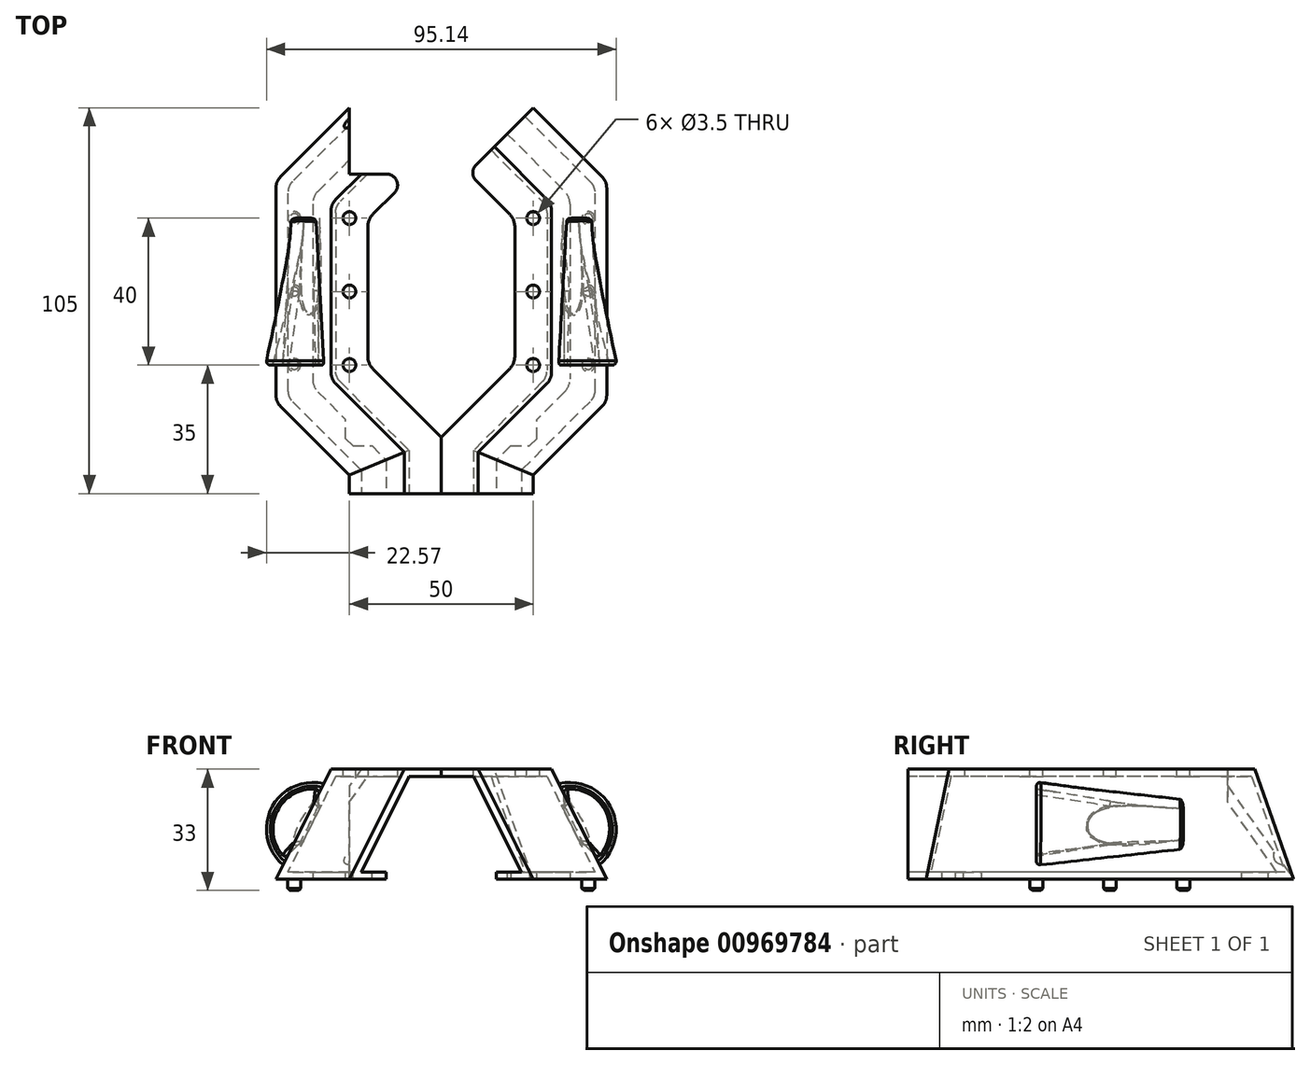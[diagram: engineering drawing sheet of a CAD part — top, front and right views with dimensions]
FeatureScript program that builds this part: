
annotation { "Feature Type Name" : "Feature", "Feature Type Description" : "" }
export const myFeature = defineFeature(function(context is Context, id is Id, definition is map)
    precondition{}
    {
        {
            var Q0;
            Q0=qCreatedBy(makeId("Front.planeOp"),FACE);
            cPlane(context, id + "F0", {"entities" : qUnion([Q0]), "cplaneType" : CPlaneType.OFFSET, "offset" : 20 * mm, "width" : 150 * mm, "height" : 150 * mm});
        }
        {
            var Q0;
            Q0=qCreatedBy(makeId("Front.planeOp"),FACE);
            cPlane(context, id + "F1", {"entities" : qUnion([Q0]), "cplaneType" : CPlaneType.OFFSET, "offset" : 20 * mm, "oppositeDirection" : true, "width" : 150 * mm, "height" : 150 * mm});
        }
        {
            var Q0;
            Q0=qCreatedBy(makeId("Top.planeOp"),FACE);
            var sketch = newSketch(context, id + "F2", { "sketchPlane" : qUnion([Q0])});
            skLineSegment(sketch, "E0.left", {"start": v(-20, 30) * mm, "end": v(-20, -30) * mm});
            skLineSegment(sketch, "E1", {"start": v(-20, 30) * mm, "end": v(0, 50) * mm});
            skLineSegment(sketch, "E2", {"start": v(-20, -30) * mm, "end": v(0, -50) * mm});
            skLineSegment(sketch, "E3", {"start": v(0, -50) * mm, "end": v(0, -55) * mm});
            skSolve(sketch);
        }
        {
            var Q0;
            Q0=qCreatedBy(makeId("Front.planeOp"),FACE);
            var sketch = newSketch(context, id + "F3", { "sketchPlane" : qUnion([Q0])});
            skLineSegment(sketch, "E4", {"start": v(-20, 0) * mm, "end": v(-5, 30) * mm});
            skLineSegment(sketch, "E5", {"start": v(-5, 30) * mm, "end": v(5, 30) * mm});
            skLineSegment(sketch, "E6", {"start": v(5, 30) * mm, "end": v(5, 28) * mm});
            skLineSegment(sketch, "E7", {"start": v(5, 28) * mm, "end": v(-3.76, 28) * mm});
            skLineSegment(sketch, "E8", {"start": v(-3.76, 28) * mm, "end": v(-16.76, 2) * mm});
            skLineSegment(sketch, "E9", {"start": v(-16.76, 2) * mm, "end": v(-10, 2) * mm});
            skLineSegment(sketch, "E10", {"start": v(-10, 2) * mm, "end": v(-10, 0) * mm});
            skLineSegment(sketch, "E11", {"start": v(-20, 0) * mm, "end": v(-10, 0) * mm});
            skSolve(sketch);
        }
        {
            var Q0;
            Q0=makeQuery(id+"F3.imprint","IMPRINT",FACE,{"disambiguationData":[TD([[makeQuery(id+"F3.imprint","IMPRINT",EDGE,{"derivedFrom":sQuery(id+"F3.wireOp",EDGE,"E4")}),-1.0]])]});
            var Q1;
            Q1=sQuery(id+"F2.wireOp",EDGE,"E0.left");
            var Q2;
            Q2=sQuery(id+"F2.wireOp",EDGE,"E1");
            var Q3;
            Q3=sQuery(id+"F2.wireOp",EDGE,"E2");
            var Q4;
            Q4=sQuery(id+"F2.wireOp",EDGE,"limmlRFK-TrjI-oLqm-ALK9-w7ykXCjVsBlW");
            var Q5;
            Q5=sQuery(id+"F2.wireOp",EDGE,"E3");
            sweep(context, id + "F4", {"profiles" : qUnion([Q0]), "path" : qUnion([Q1, Q2, Q3, Q4, Q5])});
        }
        {
            var Q0;
            Q0=qCreatedBy(id+"F0.planeOp",FACE);
            var sketch = newSketch(context, id + "F5", { "sketchPlane" : qUnion([Q0])});
            skArc(sketch, "E12", {"start": v(-6.9, 26.18) * mm, "mid": v(-21.44, 19.47) * mm, "end": v(-18.1, 3.82) * mm});
            skLineSegment(sketch, "E13", {"start": v(-6.9, 26.18) * mm, "end": v(-5, 30) * mm, "construction": true});
            skLineSegment(sketch, "E14", {"start": v(-18.1, 3.82) * mm, "end": v(-20, 0) * mm, "construction": true});
            skLineSegment(sketch, "E15", {"start": v(-6.9, 26.18) * mm, "end": v(-18.1, 3.82) * mm});
            skSolve(sketch);
        }
        {
            var Q0;
            Q0=qCreatedBy(id+"F1.planeOp",FACE);
            var sketch = newSketch(context, id + "F6", { "sketchPlane" : qUnion([Q0])});
            skArc(sketch, "E16", {"start": v(-9.15, 21.7) * mm, "mid": v(-13.4, 15.45) * mm, "end": v(-15.85, 8.3) * mm});
            skLineSegment(sketch, "E17", {"start": v(-9.15, 21.7) * mm, "end": v(-5, 30) * mm, "construction": true});
            skLineSegment(sketch, "E18", {"start": v(-15.85, 8.3) * mm, "end": v(-20, 0) * mm, "construction": true});
            skLineSegment(sketch, "E19", {"start": v(-9.15, 21.7) * mm, "end": v(-15.85, 8.3) * mm});
            skSolve(sketch);
        }
        {
            var Q0;
            Q0=makeQuery(id+"F5.imprint","IMPRINT",FACE,{"disambiguationData":[TD([[makeQuery(id+"F5.imprint","IMPRINT",EDGE,{"derivedFrom":sQuery(id+"F5.wireOp",EDGE,"E12")}),1.0]])]});
            var Q1;
            Q1=makeQuery(id+"F6.imprint","IMPRINT",FACE,{"disambiguationData":[TD([[makeQuery(id+"F6.imprint","IMPRINT",EDGE,{"derivedFrom":sQuery(id+"F6.wireOp",EDGE,"E16")}),1.0]])]});
            loft(context, id + "F7", {"operationType" : NewBodyOperationType.ADD, "sheetProfilesArray" : [{ "sheetProfileEntities" : qUnion([Q0]) }, { "sheetProfileEntities" : qUnion([Q1]) }]});
        }
        {
            var Q0;
            Q0=makeQuery(id+"F7.opLoft","CAP_FACE",FACE,{"disambiguationData":[OSD([makeQuery(id+"F5.imprint","IMPRINT",FACE,{"disambiguationData":[TD([[makeQuery(id+"F5.imprint","IMPRINT",EDGE,{"derivedFrom":sQuery(id+"F5.wireOp",EDGE,"E12")}),1.0]])]})])],"isStart":true});
            var sketch = newSketch(context, id + "F8", { "sketchPlane" : qUnion([Q0])});
            skArc(sketch, "E20", {"start": v(-7.8, 24.4) * mm, "mid": v(-19.66, 18.58) * mm, "end": v(-17.2, 5.6) * mm});
            skLineSegment(sketch, "E21", {"start": v(-17.2, 5.6) * mm, "end": v(-18.1, 3.82) * mm, "construction": true});
            skLineSegment(sketch, "E22", {"start": v(-7.8, 24.4) * mm, "end": v(-6.9, 26.18) * mm, "construction": true});
            skSolve(sketch);
        }
        {
            var Q0;
            Q0=qCreatedBy(id+"F1.planeOp",FACE);
            var sketch = newSketch(context, id + "F9", { "sketchPlane" : qUnion([Q0])});
            skArc(sketch, "E23", {"start": v(-12.05, 11.42) * mm, "mid": v(-8.48, 14.1) * mm, "end": v(-8.48, 18.58) * mm});
            skLineSegment(sketch, "E24", {"start": v(-12.05, 11.42) * mm, "end": v(-12.05, 8.3) * mm, "construction": true});
            skLineSegment(sketch, "E25", {"start": v(-8.48, 18.58) * mm, "end": v(-8.48, 21.7) * mm, "construction": true});
            skLineSegment(sketch, "E26", {"start": v(-12.05, 11.42) * mm, "end": v(-8.48, 18.58) * mm});
            skSolve(sketch);
        }
        {
            var Q1;
            {var subQ0=sQuery(id+"F8.wireOp",EDGE,"E20");Q1=makeQuery(id+"F8.imprint","IMPRINT",FACE,{"disambiguationData":[TD([[makeQuery(id+"F8.imprint","IMPRINT",EDGE,{"derivedFrom":subQ0}),1.0]])]});}
            var Q2;
            Q2=makeQuery(id+"F9.imprint","IMPRINT",FACE,{"disambiguationData":[TD([[makeQuery(id+"F9.imprint","IMPRINT",EDGE,{"derivedFrom":sQuery(id+"F9.wireOp",EDGE,"E23")}),1.0]])]});
            loft(context, id + "F10", {"operationType" : NewBodyOperationType.REMOVE, "sheetProfilesArray" : [{ "sheetProfileEntities" : qUnion([Q1]) }, { "sheetProfileEntities" : qUnion([Q2]) }]});
        }
        {
            var Q0;
            {var subQ0=sQuery(id+"F9.wireOp",EDGE,"E23");var subQ1=sQuery(id+"F9.wireOp",EDGE,"E26");var subQ2=sQuery(id+"F8.wireOp",EDGE,"E20");var subQ3=sQuery(id+"F5.wireOp",EDGE,"E15");var subQ4=sQuery(id+"F5.wireOp",EDGE,"E12");var subQ5=makeQuery(id+"F7.opLoft","MID_CAP_EDGE",EDGE,{"disambiguationData":[OSD([subQ4,subQ3]),TDD([makeQuery(id+"F5.imprint","INTERSECT",VERTEX,{"disambiguationData":[OD(0.0)],"derivedFrom":[subQ4,subQ3]}),makeQuery(id+"F5.imprint","INTERSECT",VERTEX,{"disambiguationData":[OD(1.0)],"derivedFrom":[subQ4,subQ3]}),makeQuery(id+"F5.imprint","IMPRINT",EDGE,{"derivedFrom":subQ3})])],"capPos":0.0});var subQ6=makeQuery(id+"F8.imprint","INTERSECT",VERTEX,{"disambiguationData":[OD(0.0)],"derivedFrom":[subQ5,subQ2]});var subQ7=makeQuery(id+"F8.imprint","INTERSECT",VERTEX,{"disambiguationData":[OD(1.0)],"derivedFrom":[subQ5,subQ2]});Q0=makeQuery(id+"F10.boolean.opBoolean","INTERSECT",EDGE,{"derivedFrom":[makeQuery(id+"F4.opSweep","SWEPT_FACE",FACE,{"disambiguationData":[OSD([sQuery(id+"F2.wireOp",EDGE,"E0.left"),sQuery(id+"F3.wireOp",EDGE,"E8")])]}),makeQuery(id+"F10.opLoft","SWEPT_FACE",FACE,{"disambiguationData":[OSD([subQ4,subQ3,subQ2,subQ0,subQ1]),TDD([subQ6,subQ7,makeQuery(id+"F8.imprint","IMPRINT",EDGE,{"disambiguationData":[TD([[subQ6,-1.0]])],"derivedFrom":subQ5}),makeQuery(id+"F9.imprint","INTERSECT",VERTEX,{"disambiguationData":[OD(0.0)],"derivedFrom":[subQ0,subQ1]}),makeQuery(id+"F9.imprint","INTERSECT",VERTEX,{"disambiguationData":[OD(1.0)],"derivedFrom":[subQ0,subQ1]}),makeQuery(id+"F9.imprint","IMPRINT",EDGE,{"derivedFrom":subQ0})])]})]});}
            fillet(context, id + "F11", {"entities" : qUnion([Q0]), "radius" : .32 * mm, "tangentPropagation" : true, "allowEdgeOverflow" : false});
        }
        {
            var Q0;
            Q0=makeQuery(id+"F4.opSweep","MID_CAP_EDGE",EDGE,{"disambiguationData":[OSD([sQuery(id+"F2.wireOp",VERTEX,"E2.start"),sQuery(id+"F3.wireOp",EDGE,"E4")])],"capPos":2.0});
            var Q1;
            Q1=makeQuery(id+"F4.opSweep","MID_CAP_EDGE",EDGE,{"disambiguationData":[OSD([sQuery(id+"F2.wireOp",VERTEX,"E1.start"),sQuery(id+"F3.wireOp",EDGE,"E4")])],"capPos":1.0});
            var Q2;
            Q2=makeQuery(id+"F4.opSweep","MID_CAP_EDGE",EDGE,{"disambiguationData":[OSD([sQuery(id+"F2.wireOp",VERTEX,"E2.start"),sQuery(id+"F3.wireOp",EDGE,"E6")])],"capPos":2.0});
            var Q3;
            Q3=makeQuery(id+"F4.opSweep","MID_CAP_EDGE",EDGE,{"disambiguationData":[OSD([sQuery(id+"F2.wireOp",VERTEX,"E1.start"),sQuery(id+"F3.wireOp",EDGE,"E6")])],"capPos":1.0});
            var Q4;
            Q4=makeQuery(id+"F4.opSweep","MID_CAP_EDGE",EDGE,{"disambiguationData":[OSD([sQuery(id+"F2.wireOp",VERTEX,"E1.start"),sQuery(id+"F3.wireOp",EDGE,"E10")])],"capPos":1.0});
            var Q5;
            Q5=makeQuery(id+"F4.opSweep","MID_CAP_EDGE",EDGE,{"disambiguationData":[OSD([sQuery(id+"F2.wireOp",VERTEX,"E2.start"),sQuery(id+"F3.wireOp",EDGE,"E10")])],"capPos":2.0});
            var Q6;
            Q6=makeQuery(id+"F4.opSweep","MID_CAP_EDGE",EDGE,{"disambiguationData":[OSD([sQuery(id+"F2.wireOp",VERTEX,"E2.start"),sQuery(id+"F3.wireOp",EDGE,"E8")])],"capPos":2.0});
            var Q7;
            Q7=makeQuery(id+"F4.opSweep","MID_CAP_EDGE",EDGE,{"disambiguationData":[OSD([sQuery(id+"F2.wireOp",VERTEX,"E1.start"),sQuery(id+"F3.wireOp",EDGE,"E8")])],"capPos":1.0});
            var Q8;
            {var subQ0=sQuery(id+"F6.wireOp",EDGE,"E19");var subQ1=sQuery(id+"F6.wireOp",EDGE,"E16");var subQ2=sQuery(id+"F5.wireOp",EDGE,"E15");var subQ3=sQuery(id+"F5.wireOp",EDGE,"E12");Q8=makeQuery(id+"F7.opLoft","SWEPT_EDGE",EDGE,{"disambiguationData":[OSD([subQ3,subQ2,subQ1,subQ0]),TDD([makeQuery(id+"F5.imprint","INTERSECT",VERTEX,{"disambiguationData":[OD(1.0)],"derivedFrom":[subQ3,subQ2]}),makeQuery(id+"F6.imprint","INTERSECT",VERTEX,{"disambiguationData":[OD(1.0)],"derivedFrom":[subQ1,subQ0]})])]});}
            var Q9;
            {var subQ0=sQuery(id+"F6.wireOp",EDGE,"E19");var subQ1=sQuery(id+"F6.wireOp",EDGE,"E16");var subQ2=sQuery(id+"F5.wireOp",EDGE,"E15");var subQ3=sQuery(id+"F5.wireOp",EDGE,"E12");Q9=makeQuery(id+"F7.opLoft","SWEPT_EDGE",EDGE,{"disambiguationData":[OSD([subQ3,subQ2,subQ1,subQ0]),TDD([makeQuery(id+"F5.imprint","INTERSECT",VERTEX,{"disambiguationData":[OD(0.0)],"derivedFrom":[subQ3,subQ2]}),makeQuery(id+"F6.imprint","INTERSECT",VERTEX,{"disambiguationData":[OD(0.0)],"derivedFrom":[subQ1,subQ0]})])]});}
            fillet(context, id + "F12", {"entities" : qUnion([Q0, Q1, Q2, Q3, Q4, Q5, Q6, Q7, Q8, Q9]), "radius" : 5 * mm, "tangentPropagation" : true, "allowEdgeOverflow" : false});
        }
        {
            var Q0;
            {var subQ0=sQuery(id+"F5.wireOp",EDGE,"E12");var subQ1=sQuery(id+"F5.wireOp",EDGE,"E15");Q0=makeQuery(id+"F7.opLoft","MID_CAP_EDGE",EDGE,{"disambiguationData":[OSD([subQ0,subQ1]),TDD([makeQuery(id+"F5.imprint","INTERSECT",VERTEX,{"disambiguationData":[OD(0.0)],"derivedFrom":[subQ0,subQ1]}),makeQuery(id+"F5.imprint","INTERSECT",VERTEX,{"disambiguationData":[OD(1.0)],"derivedFrom":[subQ0,subQ1]}),makeQuery(id+"F5.imprint","IMPRINT",EDGE,{"derivedFrom":subQ0})])],"capPos":0.0});}
            var Q1;
            {var subQ0=sQuery(id+"F6.wireOp",EDGE,"E16");var subQ1=sQuery(id+"F6.wireOp",EDGE,"E19");Q1=makeQuery(id+"F7.opLoft","MID_CAP_EDGE",EDGE,{"disambiguationData":[OSD([subQ0,subQ1]),TDD([makeQuery(id+"F6.imprint","INTERSECT",VERTEX,{"disambiguationData":[OD(0.0)],"derivedFrom":[subQ0,subQ1]}),makeQuery(id+"F6.imprint","INTERSECT",VERTEX,{"disambiguationData":[OD(1.0)],"derivedFrom":[subQ0,subQ1]}),makeQuery(id+"F6.imprint","IMPRINT",EDGE,{"derivedFrom":subQ0})])],"capPos":1.0});}
            var Q2;
            {var subQ0=sQuery(id+"F9.wireOp",EDGE,"E26");var subQ1=sQuery(id+"F9.wireOp",EDGE,"E23");var subQ2=sQuery(id+"F8.wireOp",EDGE,"E20");var subQ3=sQuery(id+"F5.wireOp",EDGE,"E15");var subQ4=sQuery(id+"F5.wireOp",EDGE,"E12");Q2=makeQuery(id+"F10.boolean.opBoolean","COPY",EDGE,{"derivedFrom":makeQuery(id+"F10.opLoft","SWEPT_EDGE",EDGE,{"disambiguationData":[OSD([subQ4,subQ3,subQ2,subQ1,subQ0]),TDD([makeQuery(id+"F8.imprint","INTERSECT",VERTEX,{"disambiguationData":[OD(1.0)],"derivedFrom":[makeQuery(id+"F7.opLoft","MID_CAP_EDGE",EDGE,{"disambiguationData":[OSD([subQ4,subQ3]),TDD([makeQuery(id+"F5.imprint","INTERSECT",VERTEX,{"disambiguationData":[OD(0.0)],"derivedFrom":[subQ4,subQ3]}),makeQuery(id+"F5.imprint","INTERSECT",VERTEX,{"disambiguationData":[OD(1.0)],"derivedFrom":[subQ4,subQ3]}),makeQuery(id+"F5.imprint","IMPRINT",EDGE,{"derivedFrom":subQ3})])],"capPos":0.0}),subQ2]}),makeQuery(id+"F9.imprint","INTERSECT",VERTEX,{"disambiguationData":[OD(0.0)],"derivedFrom":[subQ1,subQ0]})])]})});}
            var Q3;
            {var subQ0=sQuery(id+"F9.wireOp",EDGE,"E26");var subQ1=sQuery(id+"F9.wireOp",EDGE,"E23");var subQ2=sQuery(id+"F8.wireOp",EDGE,"E20");var subQ3=sQuery(id+"F5.wireOp",EDGE,"E15");var subQ4=sQuery(id+"F5.wireOp",EDGE,"E12");Q3=makeQuery(id+"F10.boolean.opBoolean","COPY",EDGE,{"derivedFrom":makeQuery(id+"F10.opLoft","SWEPT_EDGE",EDGE,{"disambiguationData":[OSD([subQ4,subQ3,subQ2,subQ1,subQ0]),TDD([makeQuery(id+"F8.imprint","INTERSECT",VERTEX,{"disambiguationData":[OD(0.0)],"derivedFrom":[makeQuery(id+"F7.opLoft","MID_CAP_EDGE",EDGE,{"disambiguationData":[OSD([subQ4,subQ3]),TDD([makeQuery(id+"F5.imprint","INTERSECT",VERTEX,{"disambiguationData":[OD(0.0)],"derivedFrom":[subQ4,subQ3]}),makeQuery(id+"F5.imprint","INTERSECT",VERTEX,{"disambiguationData":[OD(1.0)],"derivedFrom":[subQ4,subQ3]}),makeQuery(id+"F5.imprint","IMPRINT",EDGE,{"derivedFrom":subQ3})])],"capPos":0.0}),subQ2]}),makeQuery(id+"F9.imprint","INTERSECT",VERTEX,{"disambiguationData":[OD(1.0)],"derivedFrom":[subQ1,subQ0]})])]})});}
            fillet(context, id + "F13", {"entities" : qUnion([Q0, Q1, Q2, Q3]), "radius" : 1 * mm, "tangentPropagation" : true, "allowEdgeOverflow" : false});
        }
        {
            var Q0;
            Q0=makeQuery(id+"F4.opSweep","SWEPT_FACE",FACE,{"disambiguationData":[OSD([sQuery(id+"F2.wireOp",EDGE,"E1"),sQuery(id+"F3.wireOp",EDGE,"E5")])]});
            var sketch = newSketch(context, id + "F14", { "sketchPlane" : qUnion([Q0])});
            skCircle(sketch, "E27", {"center": v(0, 20) * mm, "radius": 1.75 * mm});
            skCircle(sketch, "E28", {"center": v(0, 0) * mm, "radius": 1.75 * mm});
            skCircle(sketch, "E29", {"center": v(0, -20) * mm, "radius": 1.75 * mm});
            skSolve(sketch);
        }
        {
            var Q0;
            Q0=makeQuery(id+"F14.imprint","IMPRINT",FACE,{"disambiguationData":[TD([[makeQuery(id+"F14.imprint","IMPRINT",EDGE,{"derivedFrom":sQuery(id+"F14.wireOp",EDGE,"E27")}),1.0]])]});
            var Q1;
            Q1=makeQuery(id+"F14.imprint","IMPRINT",FACE,{"disambiguationData":[TD([[makeQuery(id+"F14.imprint","IMPRINT",EDGE,{"derivedFrom":sQuery(id+"F14.wireOp",EDGE,"E28")}),1.0]])]});
            var Q2;
            Q2=makeQuery(id+"F14.imprint","IMPRINT",FACE,{"disambiguationData":[TD([[makeQuery(id+"F14.imprint","IMPRINT",EDGE,{"derivedFrom":sQuery(id+"F14.wireOp",EDGE,"E29")}),1.0]])]});
            var Q3;
            Q3=makeQuery(id+"F4.opSweep","SWEPT_FACE",FACE,{"disambiguationData":[OSD([sQuery(id+"F2.wireOp",EDGE,"E1"),sQuery(id+"F3.wireOp",EDGE,"E7")])]});
            extrude(context, id + "F15", {"entities" : qUnion([Q0, Q1, Q2]), "operationType" : NewBodyOperationType.REMOVE, "endBound" : BoundingType.UP_TO_SURFACE, "oppositeDirection" : true, "depth" : 25 * mm, "endBoundEntityFace" : qUnion([Q3]), "offsetDistance" : 25 * mm});
        }
        {
            var Q0;
            Q0=makeQuery(id+"F4.opSweep","SWEPT_FACE",FACE,{"disambiguationData":[OSD([sQuery(id+"F2.wireOp",EDGE,"E1"),sQuery(id+"F3.wireOp",EDGE,"E11")])]});
            var sketch = newSketch(context, id + "F16", { "sketchPlane" : qUnion([Q0])});
            skCircle(sketch, "E30", {"center": v(-15, 20) * mm, "radius": 1.75 * mm});
            skCircle(sketch, "E31", {"center": v(-15, 0) * mm, "radius": 1.75 * mm});
            skCircle(sketch, "E32", {"center": v(-15, -20) * mm, "radius": 1.75 * mm});
            skSolve(sketch);
        }
        {
            var Q0;
            Q0=makeQuery(id+"F16.imprint","IMPRINT",FACE,{"disambiguationData":[TD([[makeQuery(id+"F16.imprint","IMPRINT",EDGE,{"derivedFrom":sQuery(id+"F16.wireOp",EDGE,"E31")}),1.0]])]});
            var Q1;
            Q1=makeQuery(id+"F16.imprint","IMPRINT",FACE,{"disambiguationData":[TD([[makeQuery(id+"F16.imprint","IMPRINT",EDGE,{"derivedFrom":sQuery(id+"F16.wireOp",EDGE,"E32")}),1.0]])]});
            var Q2;
            Q2=makeQuery(id+"F16.imprint","IMPRINT",FACE,{"disambiguationData":[TD([[makeQuery(id+"F16.imprint","IMPRINT",EDGE,{"derivedFrom":sQuery(id+"F16.wireOp",EDGE,"E30")}),1.0]])]});
            var Q3;
            Q3=makeQuery(id+"F4.opSweep","SWEPT_FACE",FACE,{"disambiguationData":[OSD([sQuery(id+"F2.wireOp",EDGE,"E1"),sQuery(id+"F3.wireOp",EDGE,"E9")])]});
            extrude(context, id + "F17", {"entities" : qUnion([Q0, Q1, Q2]), "operationType" : NewBodyOperationType.ADD, "depth" : 3 * mm, "endBoundEntityFace" : qUnion([Q3]), "offsetDistance" : 25 * mm});
        }
        {
            var Q0;
            Q0=makeQuery(id+"F17.opExtrude","CAP_EDGE",EDGE,{"disambiguationData":[OSD([sQuery(id+"F16.wireOp",EDGE,"E32")])],"isStart":false});
            var Q1;
            Q1=makeQuery(id+"F17.opExtrude","CAP_EDGE",EDGE,{"disambiguationData":[OSD([sQuery(id+"F16.wireOp",EDGE,"E31")])],"isStart":false});
            var Q2;
            Q2=makeQuery(id+"F17.opExtrude","CAP_EDGE",EDGE,{"disambiguationData":[OSD([sQuery(id+"F16.wireOp",EDGE,"E30")])],"isStart":false});
            var Q3;
            Q3=makeQuery(id+"F17.opExtrude","CAP_EDGE",EDGE,{"disambiguationData":[OSD([sQuery(id+"F16.wireOp",EDGE,"E30")])],"isStart":true});
            var Q4;
            Q4=makeQuery(id+"F17.opExtrude","CAP_EDGE",EDGE,{"disambiguationData":[OSD([sQuery(id+"F16.wireOp",EDGE,"E31")])],"isStart":true});
            var Q5;
            Q5=makeQuery(id+"F17.opExtrude","CAP_EDGE",EDGE,{"disambiguationData":[OSD([sQuery(id+"F16.wireOp",EDGE,"E32")])],"isStart":true});
            chamfer(context, id + "F18", {"entities" : qUnion([Q0, Q1, Q2, Q3, Q4, Q5]), "width" : .55 * mm, "tangentPropagation" : true});
        }
        {
            var Q0;
            Q0=qCreatedBy(makeId("Right.planeOp"),FACE);
            cPlane(context, id + "F19", {"entities" : qUnion([Q0]), "cplaneType" : CPlaneType.OFFSET, "offset" : 25 * mm, "width" : 150 * mm, "height" : 150 * mm});
        }
        {
            var Q0;
            Q0=makeQuery(id+"F4.opSweep","SWEPT_BODY",BODY,{"disambiguationData":[OSD([sQuery(id+"F2.wireOp",EDGE,"E1"),sQuery(id+"F3.wireOp",EDGE,"E4"),sQuery(id+"F3.wireOp",EDGE,"E5"),sQuery(id+"F3.wireOp",EDGE,"E6"),sQuery(id+"F3.wireOp",EDGE,"E7"),sQuery(id+"F3.wireOp",EDGE,"E8"),sQuery(id+"F3.wireOp",EDGE,"E9"),sQuery(id+"F3.wireOp",EDGE,"E10"),sQuery(id+"F3.wireOp",EDGE,"E11")])]});
            var Q1;
            Q1=qCreatedBy(id+"F19.planeOp",FACE);
            mirror(context, id + "F20", {"entities" : qUnion([Q0]), "mirrorPlane" : qUnion([Q1])});
        }
        {
            var Q0;
            Q0=qCreatedBy(makeId("Top.planeOp"),FACE);
            var sketch = newSketch(context, id + "F21", { "sketchPlane" : qUnion([Q0])});
            skLineSegment(sketch, "E33.bottom", {"start": v(0, 57) * mm, "end": v(25, 57) * mm});
            skLineSegment(sketch, "E33.top", {"start": v(0, 32) * mm, "end": v(25, 32) * mm});
            skLineSegment(sketch, "E33.left", {"start": v(0, 57) * mm, "end": v(0, 32) * mm});
            skLineSegment(sketch, "E33.right", {"start": v(25, 57) * mm, "end": v(25, 32) * mm});
            skSolve(sketch);
        }
        {
            var Q0;
            Q0=makeQuery(id+"F21.imprint","IMPRINT",FACE,{"disambiguationData":[TD([[makeQuery(id+"F21.imprint","IMPRINT",EDGE,{"derivedFrom":sQuery(id+"F21.wireOp",EDGE,"E33.bottom")}),-1.0]])]});
            extrude(context, id + "F22", {"entities" : qUnion([Q0]), "operationType" : NewBodyOperationType.REMOVE, "endBound" : BoundingType.THROUGH_ALL, "depth" : 25 * mm, "offsetDistance" : 25 * mm});
        }
        {
            var Q0;
            Q0=qCreatedBy(makeId("Right.planeOp"),FACE);
            var sketch = newSketch(context, id + "F23", { "sketchPlane" : qUnion([Q0])});
            skCircle(sketch, "E34", {"center": v(70, 14) * mm, "radius": 32.5 * mm, "construction": true});
            skCircle(sketch, "E35", {"center": v(-70, 14) * mm, "radius": 32.5 * mm, "construction": true});
            skArc(sketch, "E36", {"start": v(104.79, 0) * mm, "mid": v(70, 51.5) * mm, "end": v(35.21, 0) * mm});
            skArc(sketch, "E37", {"start": v(106.94, 0) * mm, "mid": v(70, 53.5) * mm, "end": v(33.06, 0) * mm});
            skLineSegment(sketch, "E38", {"start": v(33.06, 0) * mm, "end": v(35.21, 0) * mm});
            skLineSegment(sketch, "E39", {"start": v(104.79, 0) * mm, "end": v(106.94, 0) * mm});
            skCircle(sketch, "E40", {"center": v(47, 6.5) * mm, "radius": 2.5 * mm});
            skSolve(sketch);
        }
        {
            var Q0;
            Q0=makeQuery(id+"F23.imprint","IMPRINT",FACE,{"disambiguationData":[TD([[makeQuery(id+"F23.imprint","IMPRINT",EDGE,{"derivedFrom":sQuery(id+"F23.wireOp",EDGE,"E40")}),1.0]])]});
            extrude(context, id + "F24", {"entities" : qUnion([Q0]), "operationType" : NewBodyOperationType.REMOVE, "endBound" : BoundingType.THROUGH_ALL, "oppositeDirection" : true, "depth" : 25 * mm, "offsetDistance" : 25 * mm});
        }
        {
            var Q0;
            Q0=makeQuery(id+"F22.boolean.opBoolean","INTERSECT",EDGE,{"derivedFrom":[makeQuery(id+"F4.opSweep","SWEPT_FACE",FACE,{"disambiguationData":[OSD([sQuery(id+"F2.wireOp",EDGE,"E1"),sQuery(id+"F3.wireOp",EDGE,"E6")])]}),makeQuery(id+"F22.opExtrude","SWEPT_FACE",FACE,{"disambiguationData":[OSD([sQuery(id+"F21.wireOp",EDGE,"E33.top")])]})]});
            var Q1;
            Q1=makeQuery(id+"F20.opPattern","COPY",EDGE,{"derivedFrom":makeQuery(id+"F4.opSweep","CAP_EDGE",EDGE,{"disambiguationData":[OSD([sQuery(id+"F2.wireOp",VERTEX,"E1.end"),sQuery(id+"F3.wireOp",EDGE,"E6")])],"isStart":true}),"instanceName":"1"});
            fillet(context, id + "F25", {"entities" : qUnion([Q0, Q1]), "radius" : 3 * mm, "tangentPropagation" : true, "allowEdgeOverflow" : false});
        }
        {
            var Q0;
            Q0=makeQuery(id+"F4.opSweep","SWEPT_FACE",FACE,{"disambiguationData":[OSD([sQuery(id+"F2.wireOp",EDGE,"E1"),sQuery(id+"F3.wireOp",EDGE,"E11")])]});
            var sketch = newSketch(context, id + "F26", { "sketchPlane" : qUnion([Q0])});
            skLineSegment(sketch, "E41.bottom", {"start": v(-1, 42) * mm, "end": v(51, 42) * mm});
            skLineSegment(sketch, "E41.top", {"start": v(-1, 30) * mm, "end": v(51, 30) * mm});
            skLineSegment(sketch, "E41.left", {"start": v(-1, 42) * mm, "end": v(-1, 30) * mm});
            skLineSegment(sketch, "E41.right", {"start": v(51, 42) * mm, "end": v(51, 30) * mm});
            skPoint(sketch, "E41.middle", {"position": v(25, 36) * mm});
            skSolve(sketch);
        }
        {
            var Q0;
            {var subQ7=sQuery(id+"F26.wireOp",EDGE,"E41.right");Q0=makeQuery(id+"F26.imprint","IMPRINT",FACE,{"disambiguationData":[TD([[makeQuery(id+"F26.imprint","IMPRINT",EDGE,{"derivedFrom":subQ7}),-1.0]])]});}
            var Q1;
            {var subQ0=sQuery(id+"F26.wireOp",EDGE,"E41.left");Q1=makeQuery(id+"F26.imprint","IMPRINT",FACE,{"disambiguationData":[TD([[makeQuery(id+"F26.imprint","IMPRINT",EDGE,{"derivedFrom":subQ0}),1.0]])]});}
            var Q2;
            Q2=makeQuery(id+"F4.opSweep","SWEPT_FACE",FACE,{"disambiguationData":[OSD([sQuery(id+"F2.wireOp",EDGE,"E1"),sQuery(id+"F3.wireOp",EDGE,"E9")])]});
            extrude(context, id + "F27", {"entities" : qUnion([Q0, Q1]), "operationType" : NewBodyOperationType.REMOVE, "endBound" : BoundingType.UP_TO_SURFACE, "oppositeDirection" : true, "depth" : 25 * mm, "endBoundEntityFace" : qUnion([Q2]), "offsetDistance" : 25 * mm});
        }
        {
            var Q0;
            Q0=makeQuery(id+"F27.boolean.opBoolean","COPY",EDGE,{"derivedFrom":makeQuery(id+"F27.opExtrude","SWEPT_EDGE",EDGE,{"disambiguationData":[OSD([sQuery(id+"F26.wireOp",EDGE,"E41.bottom"),sQuery(id+"F26.wireOp",EDGE,"E41.left")])]})});
            var Q1;
            Q1=makeQuery(id+"F27.boolean.opBoolean","COPY",EDGE,{"derivedFrom":makeQuery(id+"F27.opExtrude","SWEPT_EDGE",EDGE,{"disambiguationData":[OSD([sQuery(id+"F26.wireOp",EDGE,"E41.bottom"),sQuery(id+"F26.wireOp",EDGE,"E41.right")])]})});
            chamfer(context, id + "F28", {"entities" : qUnion([Q0, Q1]), "width" : 2 * mm, "tangentPropagation" : true});
        }
    });
